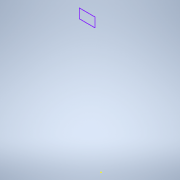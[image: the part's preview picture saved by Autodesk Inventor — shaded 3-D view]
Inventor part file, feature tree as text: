
AUTODESK INVENTOR PART (.ipt)
format: ipt  version: 2020 (Build 240168000, 168)  size: 91,648 bytes
history: native  units: mm
features: other x1, extrude x1, sketch x1
ambient origin geometry x8: Origin, YZ Plane, XZ Plane, XY Plane, X Axis, Y Axis, Z Axis, Center Point
bodies: Body1 (feature_tree)
feature tree (3):
  other  "Sólido1"
  extrude  "Extrusão1"  [1 undecoded]
  sketch  "Esboço1"  dims[d0=66.1mm d1=0.0mm]
note: 1 required parameter value undecoded (feature->parameter linkage not recoverable at this tier; creation-order binding heuristic only, values carry confidence <= 0.55)
